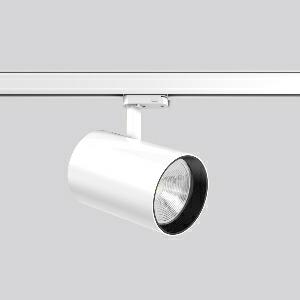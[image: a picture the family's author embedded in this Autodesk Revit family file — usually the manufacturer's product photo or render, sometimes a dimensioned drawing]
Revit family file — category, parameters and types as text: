
# Revit family: deecos_s_maxi_742238_002_8dca
name_source: partatom
category: Lighting Fixtures
units: mm (PartAtom-declared; Revit-internal decimal feet)

## family parameters
Cut with Voids When Loaded = No
Host = Face
Light Source = No
Part Type = Normal
Room Calculation Point = No
Round Connector Dimension = Use Diameter
Shared = No

## types (1)
- DEECOS S maxi (1 x LED Modul 920 meat+, 1900 lm, 2000)
    Apparent Load = 33 VA
    Approval mark = CE
    CIE Flux Codes = 97 100 100 100 100
    Color Rendering = 90
    Color Temperature = 2000
    Default Elevation = 1800 mm
    Description = Series: DEECOS S maxi
LED surface-mounted projector in modern design with no visible cooling ribs. Housing: die-cast aluminium, powder-coated. Rotation range: 356°. Swivel range: 90°. Black plastic ring and recessed LED to prevent glare from the side. Optical assembly with lens made of plastic (polycarbonate) for the best homogeneous light distribution - can be changed without tools. Special LED for illumination of meat included. With multi adaptor for 3-circuit tracks 230 V. Suitable for Track on ceiling, Wall track. High quality converter without flickering and stroboscopic effect. The following accessories can be mounted without use of tools: interchangeable lenses, decorative glasses, honeycomb louvre, clear and frosted diffusers, white interchangeable plastic ring. 
Colour: traffic white, matt (RAL 9016)
Diameter: 123 mm
Height: 200 mm
Lamp: LED
Socket: without socket
Colour temperature: meat +
System power: 33 W
Rated luminous flux: 1900 lm
Luminous efficiency: 58 lm/W
Control gear: Regulated power supply
Protection class: I
Type of protection: IP 20
    Height = 200 mm  [stored 0.656168 ft]
    Lamp = 1 x LED Modul 920 meat+
    Lamp Light Flux = 1900 lm
    Lamp count = 1
    Length = 123 mm
    Lifetime = 50000 h
    Luminous efficacy = 58 lm/W
    Manufacturer = RZB
    ModVariant = No
    Model = 742238.002
    Mounting Place = Ceiling
    Mounting Type = Rail mounted
    Number of Poles = 1
    OnlyDefault = Yes
    Power Factor = 1
    Product Name = DEECOS S maxi
    Product group = Track mounted projectors
    ProductGroupID = 301
    Protection Class = Protection class I
    Protection Degree = IP 20
    RLX_Detail_Level = 1
    RLX_Emergency_Light_Flux = 0 lm
    RLX_Emergency_Type = 0
    RLX_Emergency_Type_DB = No
    RlxData = <blob elided: 39409 chars, md5=eda4d91b>
    Socket = socket
    Standby Power = 0 W
    System Light Flux = 1900 lm
    System Power = 33 W
    Type Comments = Product without accessories
    Type Image = 741958.002.jpg
    URL = http://relux.com
    VarID = ---
    Voltage = 230 V
    Voltage Range = 220-240 V
    Weight = 0.00 kg
    Width = 0 mm  [stored 0 ft]

note: [stored X ft] marks values corroborated as IEEE doubles in the binary element streams (Revit-internal decimal feet)

## geometry (parser evidence)
native form markers: Blend x4, Sweep x14
no freeform markers — native parametric forms only
